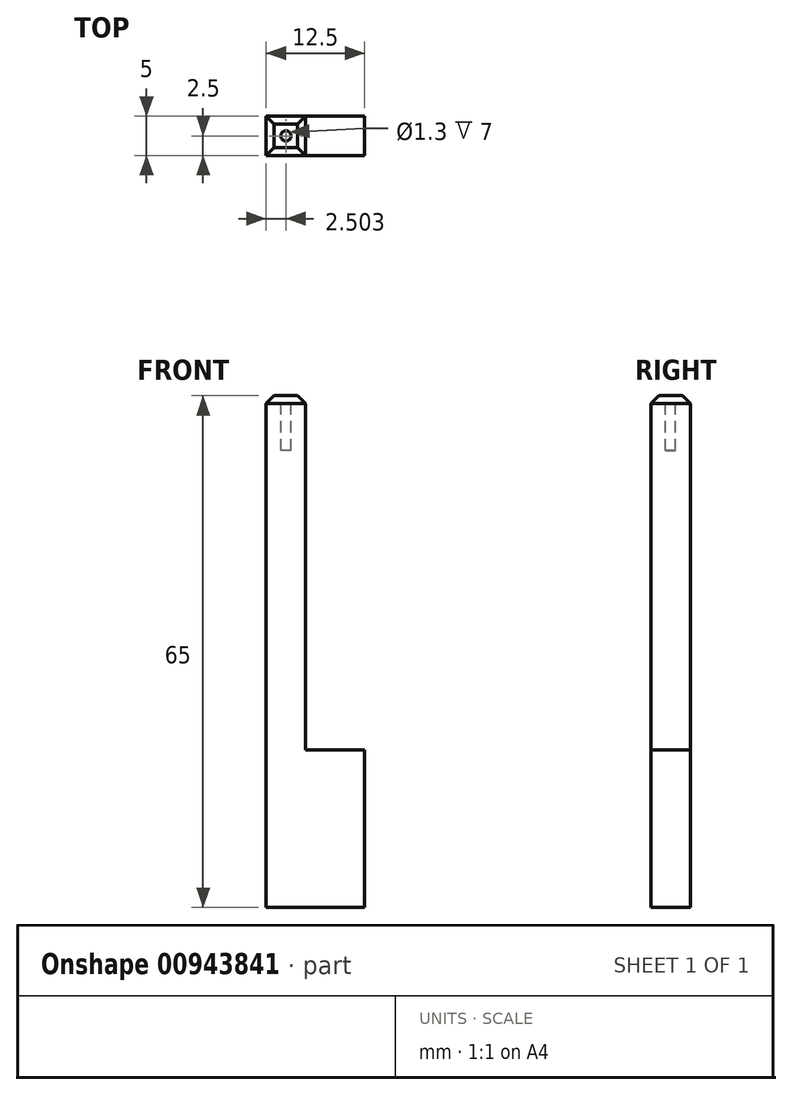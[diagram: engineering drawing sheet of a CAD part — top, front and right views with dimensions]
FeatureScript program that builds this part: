
annotation { "Feature Type Name" : "Feature", "Feature Type Description" : "" }
export const myFeature = defineFeature(function(context is Context, id is Id, definition is map)
    precondition{}
    {
        {
            var Q0;
            Q0=qCreatedBy(makeId("Front.planeOp"),FACE);
            var sketch = newSketch(context, id + "F0", { "sketchPlane" : qUnion([Q0])});
            skLineSegment(sketch, "E0.bottom", {"start": v(-41.92, 60.55) * mm, "end": v(-36.92, 60.55) * mm});
            skLineSegment(sketch, "E0.top", {"start": v(-41.92, -4.45) * mm, "end": v(-36.92, -4.45) * mm});
            skLineSegment(sketch, "E0.left", {"start": v(-41.92, 60.55) * mm, "end": v(-41.92, -4.45) * mm});
            skLineSegment(sketch, "E0.right", {"start": v(-36.92, 60.55) * mm, "end": v(-36.92, 15.55) * mm});
            skLineSegment(sketch, "E1.bottom", {"start": v(-36.92, -4.45) * mm, "end": v(-29.42, -4.45) * mm});
            skLineSegment(sketch, "E1.top", {"start": v(-36.92, 15.55) * mm, "end": v(-29.42, 15.55) * mm});
            skLineSegment(sketch, "E1.right", {"start": v(-29.42, -4.45) * mm, "end": v(-29.42, 15.55) * mm});
            skSolve(sketch);
        }
        {
            var Q0;
            Q0 = qSketchRegion(id + "F0", true);
            extrude(context, id + "F1", {"entities" : qUnion([Q0]), "depth" : 5 * mm, "offsetDistance" : 25 * mm});
        }
        {
            var Q0;
            Q0=makeQuery(id+"F1.opExtrude","SWEPT_FACE",FACE,{"disambiguationData":[OSD([sQuery(id+"F0.wireOp",EDGE,"E0.bottom")])]});
            var sketch = newSketch(context, id + "F2", { "sketchPlane" : qUnion([Q0])});
            skCircle(sketch, "E2", {"center": v(-39.42, -2.5) * mm, "radius": 0.65 * mm});
            skPoint(sketch, "E2.centerSnap0", {"position": v(-39.42, 0) * mm});
            skPoint(sketch, "E2.centerSnap1", {"position": v(-41.92, -2.5) * mm});
            skSolve(sketch);
        }
        {
            var Q0;
            Q0 = qSketchRegion(id + "F2", true);
            extrude(context, id + "F3", {"entities" : qUnion([Q0]), "operationType" : NewBodyOperationType.REMOVE, "oppositeDirection" : true, "depth" : 7 * mm, "offsetDistance" : 25 * mm});
        }
        {
            var Q0;
            Q0=makeQuery(id+"F1.opExtrude","SWEPT_EDGE",EDGE,{"disambiguationData":[OSD([sQuery(id+"F0.wireOp",EDGE,"E0.bottom"),sQuery(id+"F0.wireOp",EDGE,"E0.right")])]});
            var Q1;
            Q1=makeQuery(id+"F1.opExtrude","CAP_EDGE",EDGE,{"disambiguationData":[OSD([sQuery(id+"F0.wireOp",EDGE,"E0.bottom")])],"isStart":false});
            var Q2;
            Q2=makeQuery(id+"F1.opExtrude","CAP_EDGE",EDGE,{"disambiguationData":[OSD([sQuery(id+"F0.wireOp",EDGE,"E0.bottom")])],"isStart":true});
            var Q3;
            Q3=makeQuery(id+"F1.opExtrude","SWEPT_EDGE",EDGE,{"disambiguationData":[OSD([sQuery(id+"F0.wireOp",EDGE,"E0.bottom"),sQuery(id+"F0.wireOp",EDGE,"E0.left")])]});
            chamfer(context, id + "F4", {"entities" : qUnion([Q0, Q1, Q2, Q3]), "width" : 1 * mm, "tangentPropagation" : true});
        }
    });
